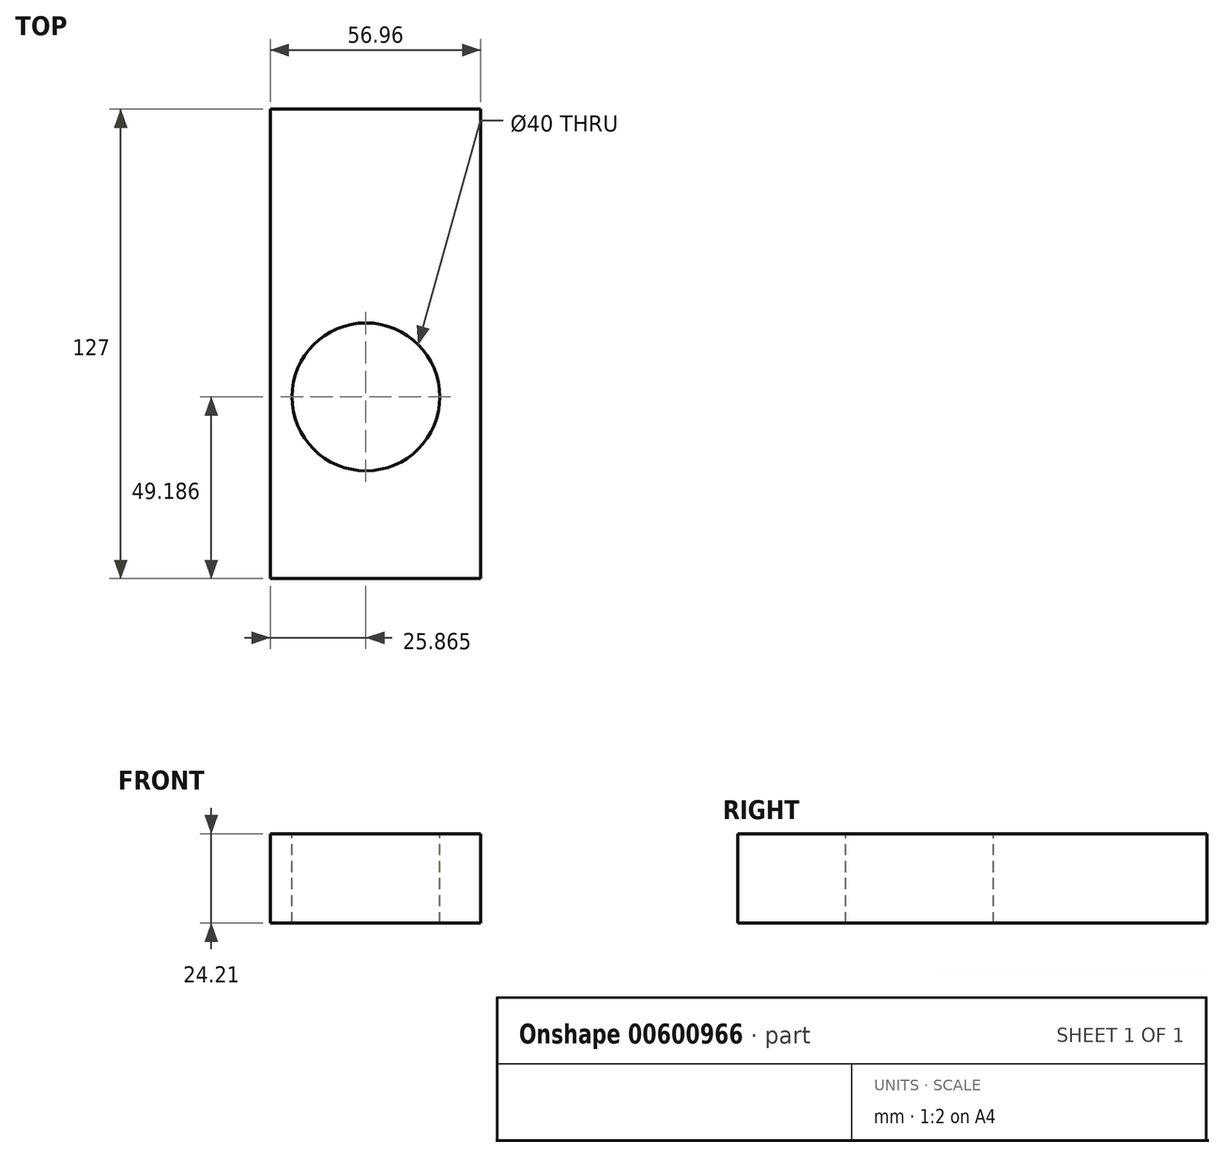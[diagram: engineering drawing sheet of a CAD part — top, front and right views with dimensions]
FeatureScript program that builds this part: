
annotation { "Feature Type Name" : "Feature", "Feature Type Description" : "" }
export const myFeature = defineFeature(function(context is Context, id is Id, definition is map)
    precondition{}
    {
        {
            var Q0;
            Q0=qCreatedBy(makeId("Front.planeOp"),FACE);
            var sketch = newSketch(context, id + "F0", { "sketchPlane" : qUnion([Q0])});
            skLineSegment(sketch, "E0.bottom", {"start": v(-86.8, 24.21) * mm, "end": v(-29.83, 24.21) * mm});
            skLineSegment(sketch, "E0.top", {"start": v(-86.8, 0) * mm, "end": v(-29.83, 0) * mm});
            skLineSegment(sketch, "E0.left", {"start": v(-86.8, 24.21) * mm, "end": v(-86.8, 0) * mm});
            skLineSegment(sketch, "E0.right", {"start": v(-29.83, 24.21) * mm, "end": v(-29.83, 0) * mm});
            skSolve(sketch);
        }
        {
            var Q0;
            Q0=makeQuery(id+"F0.imprint","IMPRINT",FACE,{"disambiguationData":[TD([[makeQuery(id+"F0.imprint","IMPRINT",EDGE,{"derivedFrom":sQuery(id+"F0.wireOp",EDGE,"E0.bottom")}),-1.0]])]});
            extrude(context, id + "F1", {"entities" : qUnion([Q0]), "depth" : 127 * mm, "offsetDistance" : 25.4 * mm});
        }
        {
            var Q0;
            Q0=makeQuery(id+"F1.opExtrude","SWEPT_FACE",FACE,{"disambiguationData":[OSD([sQuery(id+"F0.wireOp",EDGE,"E0.bottom")])]});
            var sketch = newSketch(context, id + "F2", { "sketchPlane" : qUnion([Q0])});
            skCircle(sketch, "E1", {"center": v(-60.92, -77.81) * mm, "radius": 20 * mm});
            skSolve(sketch);
        }
        {
            var Q0;
            Q0=makeQuery(id+"F2.imprint","IMPRINT",FACE,{"disambiguationData":[TD([[makeQuery(id+"F2.imprint","IMPRINT",EDGE,{"derivedFrom":sQuery(id+"F2.wireOp",EDGE,"E1")}),1.0]])]});
            extrude(context, id + "F3", {"entities" : qUnion([Q0]), "operationType" : NewBodyOperationType.REMOVE, "oppositeDirection" : true, "depth" : 25 * mm, "offsetDistance" : 25 * mm});
        }
    });
